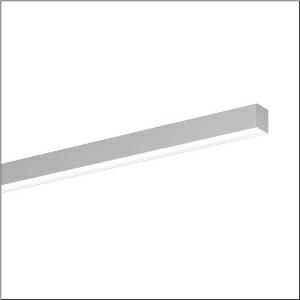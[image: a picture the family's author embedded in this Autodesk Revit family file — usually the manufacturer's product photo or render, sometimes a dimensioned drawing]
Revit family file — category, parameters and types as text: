
# Revit family: silica_r__21_51mx23tat4s_c658
name_source: partatom
category: Lighting Fixtures
units: mm (PartAtom-declared; Revit-internal decimal feet)

## family parameters
Cut with Voids When Loaded = No
Host = Face
Light Source = No
Part Type = Normal
Room Calculation Point = No
Round Connector Dimension = Use Diameter
Shared = No

## types (1)
- --- (1 x LED, 3230 lm, 32.4 W, 6500K)
    Apparent Load = 32 VA
    CIE Flux Codes = 78 96 99 100 100
    Color Rendering = 80
    Color Temperature = 6500K
    Default Elevation = 1800 mm
    Description = Silica® 21, office luminaire, primary optical cover: prismatic diffuser, of PMMA, CAT 2 (L<= 3000cd/m²), light emission: direct distribution, primary light characteristic: symmetric, installation type: surface-mounted, LED, rated luminous flux: 3.230lm, luminous efficacy: 95lm/W, light colour: 8tw, colour temperature: 2700..6500K, control gear: DALI DT8, with terminal, 3+2-pole, max. 2.5mm², mains connection: 220..240V, AC, 50/60Hz, rated input power: 34W, luminaire housing, of aluminium, metallic grey (RAL 9006), length: 1.204mm, width: 53mm, height: 53mm, protection rating (complete): IP20, insulation class (complete): insulation class I (protective earthing), certification: CE, permissible operating ambient temperature: 0..+35°C, standard: EN 50419, packaging unit: 1 piece
    Height = 53 mm
    Lamp = 1 x LED
    Lamp Light Flux = 3230 lm
    Lamp Power = 32.4 W
    Lamp count = 1
    Length = 1204 mm
    Luminous efficacy = 100 lm/W
    Manufacturer = Siteco
    ModVariant = No
    Model = 51MX23TAT4S
    Mounting Place = Ceiling
    Mounting Type = Surface mounted
    Number of Poles = 1
    OnlyDefault = Yes
    Power Factor = 1
    Product Name = Silica® 21
    Product group = office luminaire | ceiling mounted
    ProductGroupID = 302
    Protection Class = Protection class I
    Protection Degree = IP 20
    RLX_Detail_Level = 1
    RLX_Emergency_Light_Flux = 0 lm
    RLX_Emergency_Type = 0
    RLX_Emergency_Type_DB = No
    RlxData = <blob elided: 18041 chars, md5=4f16db9d>
    Socket = socket
    Standby Power = 0 W
    System Light Flux = 3230 lm
    System Power = 32 W
    Type Comments = individual setting
    Type Image = l_1335933.jpg
    URL = http://relux.com
    VarID = @adj_139800
    Voltage = 0 V
    Weight = 0.00 kg
    Width = 53 mm

## geometry (parser evidence)
native form markers: Blend x4, Sweep x11
no freeform markers — native parametric forms only
